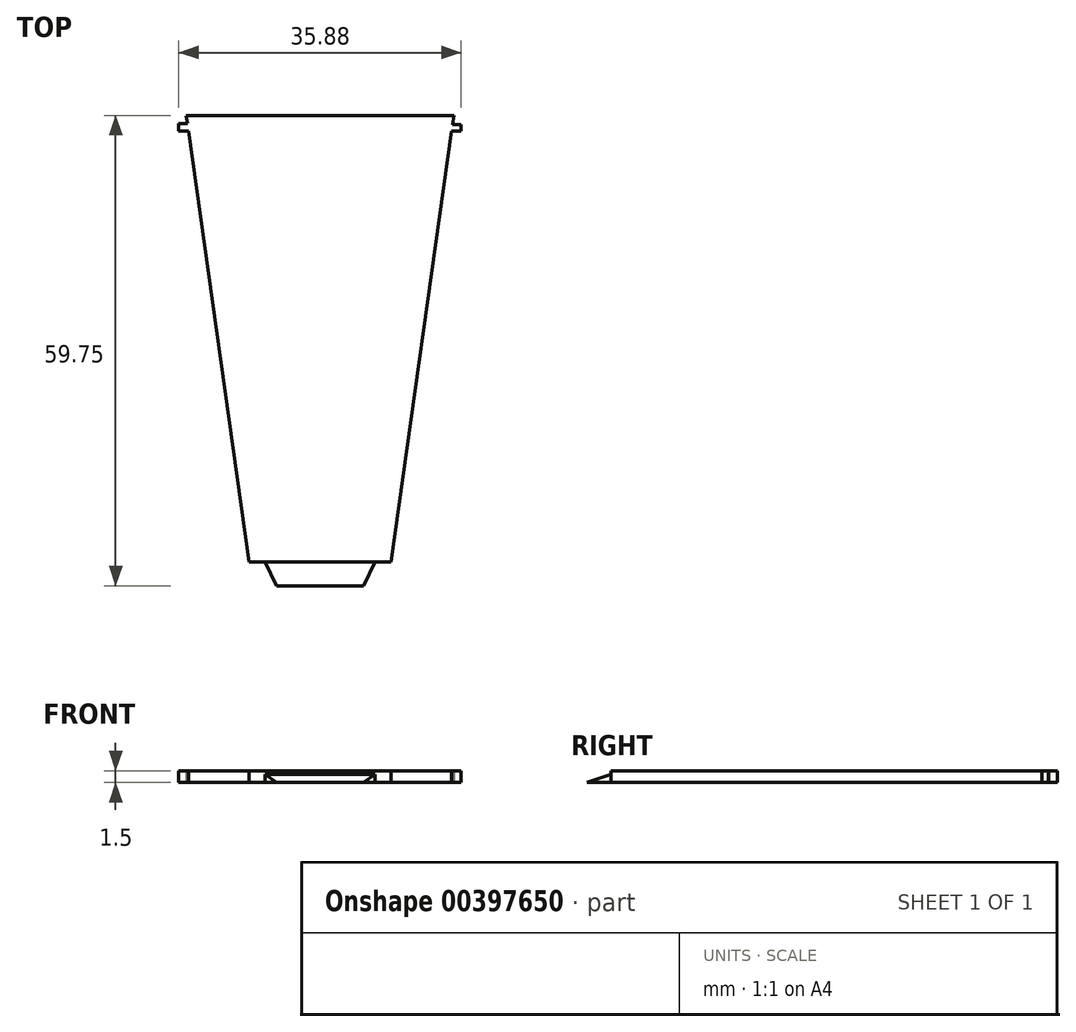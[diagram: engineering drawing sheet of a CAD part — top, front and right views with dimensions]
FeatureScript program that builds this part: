
annotation { "Feature Type Name" : "Feature", "Feature Type Description" : "" }
export const myFeature = defineFeature(function(context is Context, id is Id, definition is map)
    precondition{}
    {
        {
            var Q0;
            Q0=qCreatedBy(makeId("Top.planeOp"),FACE);
            var sketch = newSketch(context, id + "F0", { "sketchPlane" : qUnion([Q0])});
            skLineSegment(sketch, "E0", {"start": v(0, 27.6) * mm, "end": v(0, -29.14) * mm});
            skLineSegment(sketch, "E1", {"start": v(0, 27.6) * mm, "end": v(17, 27.6) * mm});
            skLineSegment(sketch, "E2", {"start": v(0, -29.14) * mm, "end": v(9, -29.14) * mm});
            skLineSegment(sketch, "E3.MirrorCS", {"start": v(0, 27.6) * mm, "end": v(-17, 27.6) * mm});
            skLineSegment(sketch, "E4.MirrorCS", {"start": v(0, -29.14) * mm, "end": v(-9, -29.14) * mm});
            skLineSegment(sketch, "E5", {"start": v(-17, 27.6) * mm, "end": v(-9, -29.14) * mm});
            skLineSegment(sketch, "E6", {"start": v(17, 27.6) * mm, "end": v(9, -29.14) * mm});
            skLineSegment(sketch, "E7", {"start": v(0, -29.14) * mm, "end": v(7, -29.14) * mm});
            skLineSegment(sketch, "E8", {"start": v(0, -29.14) * mm, "end": v(-7, -29.14) * mm});
            skSolve(sketch);
        }
        {
            var Q0;
            Q0 = qSketchRegion(id + "F0", true);
            extrude(context, id + "F1", {"entities" : qUnion([Q0]), "depth" : 1.5 * mm});
        }
        {
            var Q0;
            Q0=makeQuery(id+"F1.opExtrude","CAP_FACE",FACE,{"disambiguationData":[OSD([sQuery(id+"F0.wireOp",EDGE,"E1"),sQuery(id+"F0.wireOp",EDGE,"E2"),sQuery(id+"F0.wireOp",EDGE,"E3.MirrorCS"),sQuery(id+"F0.wireOp",EDGE,"E4.MirrorCS"),sQuery(id+"F0.wireOp",EDGE,"E5"),sQuery(id+"F0.wireOp",EDGE,"E6"),sQuery(id+"F0.wireOp",EDGE,"E7"),sQuery(id+"F0.wireOp",EDGE,"E8")])],"isStart":true});
            var sketch = newSketch(context, id + "F2", { "sketchPlane" : qUnion([Q0])});
            skLineSegment(sketch, "E9", {"start": v(0, 29.14) * mm, "end": v(-7, 29.14) * mm});
            skLineSegment(sketch, "E10", {"start": v(0, 29.14) * mm, "end": v(-5.5, 29.14) * mm});
            skLineSegment(sketch, "E11", {"start": v(-5.5, 29.14) * mm, "end": v(-5.5, 32.14) * mm});
            skLineSegment(sketch, "E12", {"start": v(-7, 29.14) * mm, "end": v(-5.5, 32.14) * mm});
            skLineSegment(sketch, "E13", {"start": v(-5.5, 32.14) * mm, "end": v(0, 32.14) * mm});
            skLineSegment(sketch, "E14.MirrorCS", {"start": v(5.5, 32.14) * mm, "end": v(0, 32.14) * mm});
            skLineSegment(sketch, "E15.MirrorCS", {"start": v(7, 29.14) * mm, "end": v(5.5, 32.14) * mm});
            skLineSegment(sketch, "E16.MirrorCS", {"start": v(0, 29.14) * mm, "end": v(5.5, 29.14) * mm});
            skLineSegment(sketch, "E17.MirrorCS", {"start": v(0, 29.14) * mm, "end": v(7, 29.14) * mm});
            skSolve(sketch);
        }
        {
            var Q0;
            Q0 = qSketchRegion(id + "F2", true);
            extrude(context, id + "F3", {"entities" : qUnion([Q0]), "oppositeDirection" : true, "depth" : 1 * mm});
        }
        {
            var Q0;
            Q0=makeQuery(id+"F3.opExtrude","CAP_EDGE",EDGE,{"disambiguationData":[OSD([sQuery(id+"F2.wireOp",EDGE,"E13"),sQuery(id+"F2.wireOp",EDGE,"E14.MirrorCS")])],"isStart":false});
            chamfer(context, id + "F4", {"entities" : qUnion([Q0]), "chamferType" : ChamferType.TWO_OFFSETS, "width1" : 1 * mm, "oppositeDirection" : false, "width2" : 3 * mm, "tangentPropagation" : true});
        }
        {
            var Q0;
            Q0=makeQuery(id+"F1.opExtrude","CAP_FACE",FACE,{"disambiguationData":[OSD([sQuery(id+"F0.wireOp",EDGE,"E1"),sQuery(id+"F0.wireOp",EDGE,"E2"),sQuery(id+"F0.wireOp",EDGE,"E3.MirrorCS"),sQuery(id+"F0.wireOp",EDGE,"E4.MirrorCS"),sQuery(id+"F0.wireOp",EDGE,"E5"),sQuery(id+"F0.wireOp",EDGE,"E6"),sQuery(id+"F0.wireOp",EDGE,"E7"),sQuery(id+"F0.wireOp",EDGE,"E8")])],"isStart":true});
            var sketch = newSketch(context, id + "F5", { "sketchPlane" : qUnion([Q0])});
            skLineSegment(sketch, "E18.bottom", {"start": v(-15.4, -25.61) * mm, "end": v(-17.96, -25.61) * mm});
            skLineSegment(sketch, "E18.top", {"start": v(-15.4, -26.58) * mm, "end": v(-17.96, -26.58) * mm});
            skLineSegment(sketch, "E18.left", {"start": v(-15.4, -25.61) * mm, "end": v(-15.4, -26.58) * mm});
            skLineSegment(sketch, "E18.right", {"start": v(-17.96, -25.61) * mm, "end": v(-17.96, -26.58) * mm});
            skLineSegment(sketch, "E19.bottom", {"start": v(14.71, -25.61) * mm, "end": v(17.92, -25.61) * mm});
            skLineSegment(sketch, "E19.top", {"start": v(14.71, -26.43) * mm, "end": v(17.92, -26.43) * mm});
            skLineSegment(sketch, "E19.left", {"start": v(14.71, -25.61) * mm, "end": v(14.71, -26.43) * mm});
            skPoint(sketch, "E20.bottom.start.orphan", {"position": v(15.04, -25.1) * mm});
            skPoint(sketch, "E21.left.end.orphan", {"position": v(-15.85, -25.1) * mm});
            skLineSegment(sketch, "E22", {"start": v(17.92, -25.61) * mm, "end": v(17.92, -26.43) * mm});
            skPoint(sketch, "E23.orphan", {"position": v(18.35, -26.43) * mm});
            skSolve(sketch);
        }
        {
            var Q0;
            Q0 = qSketchRegion(id + "F5", true);
            extrude(context, id + "F6", {"entities" : qUnion([Q0]), "operationType" : NewBodyOperationType.ADD, "oppositeDirection" : true, "depth" : 1.5 * mm});
        }
        {
            var Q0;
            Q0 = qSketchRegion(id + "F5", true);
            extrude(context, id + "F7", {"entities" : qUnion([Q0]), "operationType" : NewBodyOperationType.ADD, "oppositeDirection" : true, "depth" : 1.5 * mm});
        }
    });
